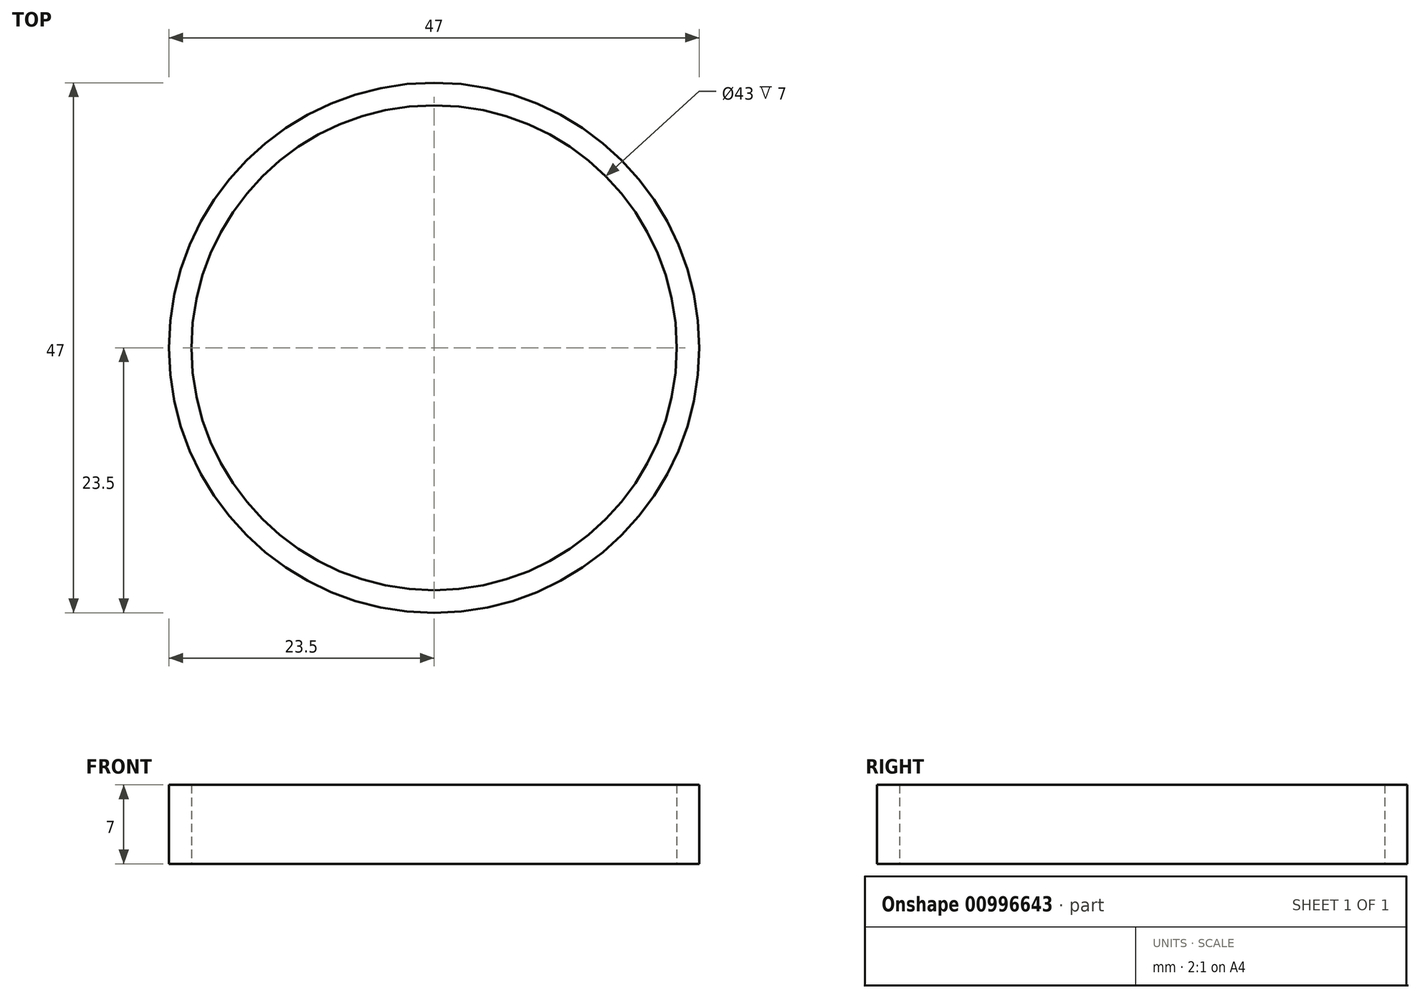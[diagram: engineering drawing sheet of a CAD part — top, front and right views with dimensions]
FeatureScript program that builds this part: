
annotation { "Feature Type Name" : "Feature", "Feature Type Description" : "" }
export const myFeature = defineFeature(function(context is Context, id is Id, definition is map)
    precondition{}
    {
        {
            var Q0;
            Q0=qCreatedBy(makeId("Top.planeOp"),FACE);
            var sketch = newSketch(context, id + "F0", { "sketchPlane" : qUnion([Q0])});
            skCircle(sketch, "E0", {"center": v(0, 0) * mm, "radius": 21.5 * mm});
            skCircle(sketch, "E1", {"center": v(0, 0) * mm, "radius": 23.5 * mm});
            skSolve(sketch);
        }
        {
            var Q0;
            Q0=makeQuery(id+"F0.imprint","IMPRINT",FACE,{"disambiguationData":[TD([[makeQuery(id+"F0.imprint","IMPRINT",EDGE,{"derivedFrom":sQuery(id+"F0.wireOp",EDGE,"E0")}),-1.0]])]});
            extrude(context, id + "F1", {"entities" : qUnion([Q0]), "depth" : 7 * mm, "offsetDistance" : 25 * mm});
        }
    });
